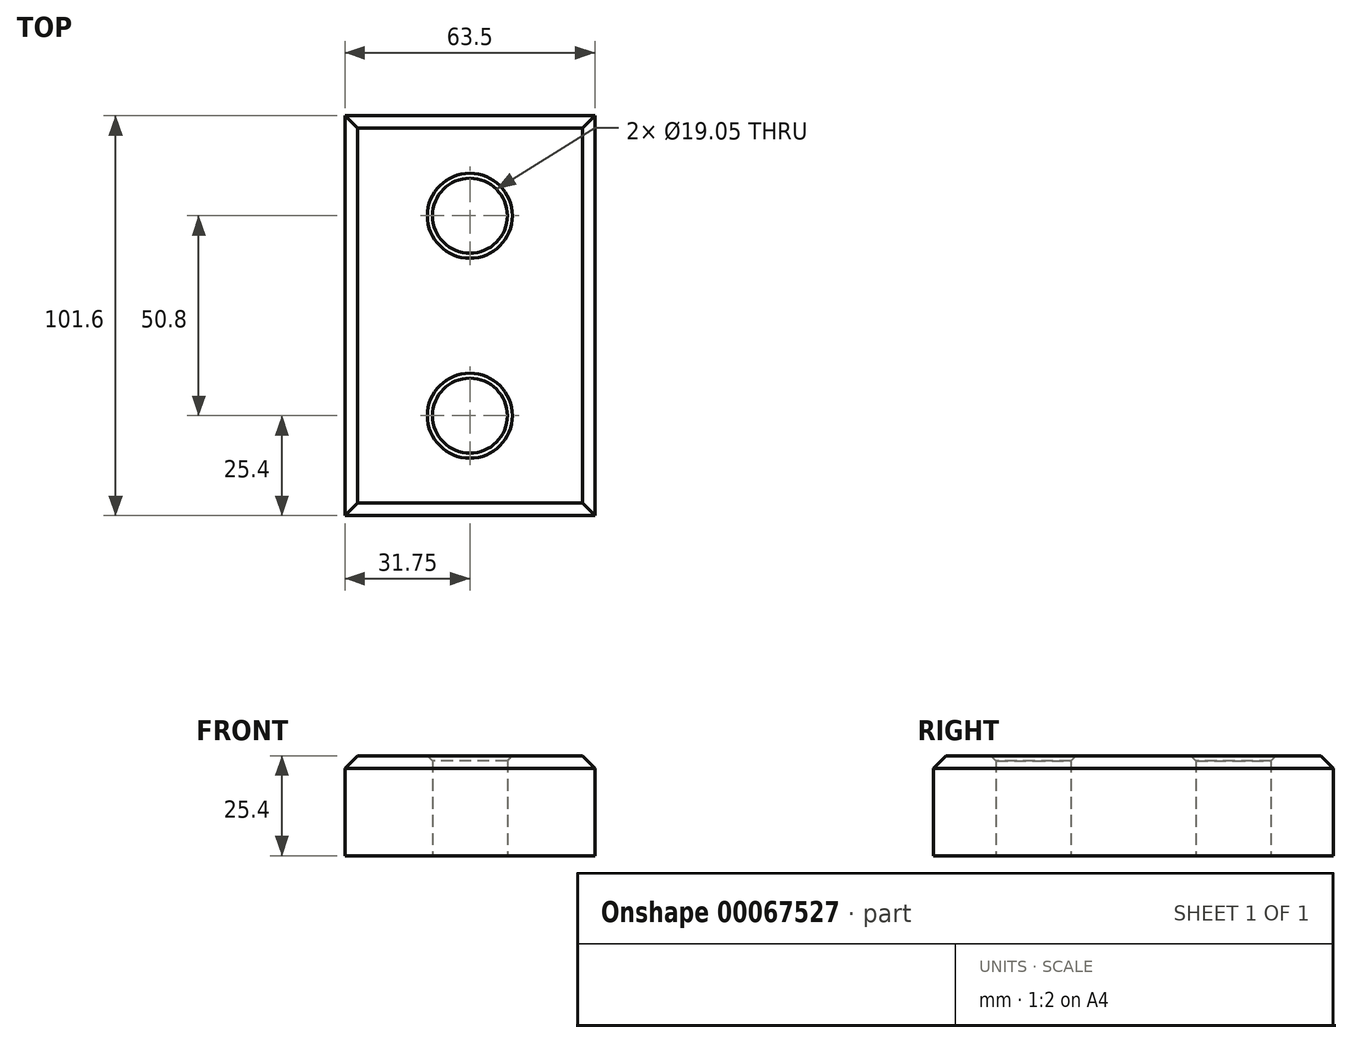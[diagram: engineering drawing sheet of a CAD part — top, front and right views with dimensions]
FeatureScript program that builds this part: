
annotation { "Feature Type Name" : "Feature", "Feature Type Description" : "" }
export const myFeature = defineFeature(function(context is Context, id is Id, definition is map)
    precondition{}
    {
        {
            var Q0;
            Q0=qCreatedBy(makeId("Top.planeOp"),FACE);
            var sketch = newSketch(context, id + "F0", { "sketchPlane" : qUnion([Q0])});
            skLineSegment(sketch, "E0.bottom", {"start": v(0, 0) * mm, "end": v(63.5, 0) * mm});
            skLineSegment(sketch, "E0.top", {"start": v(0, 101.6) * mm, "end": v(63.5, 101.6) * mm});
            skLineSegment(sketch, "E0.left", {"start": v(0, 0) * mm, "end": v(0, 101.6) * mm});
            skLineSegment(sketch, "E0.right", {"start": v(63.5, 0) * mm, "end": v(63.5, 101.6) * mm});
            skCircle(sketch, "E1", {"center": v(31.75, 76.2) * mm, "radius": 9.53 * mm});
            skCircle(sketch, "E2", {"center": v(31.75, 25.4) * mm, "radius": 9.53 * mm});
            skSolve(sketch);
        }
        {
            var Q0;
            Q0=makeQuery(id+"F0.imprint","IMPRINT",FACE,{"disambiguationData":[TD([[makeQuery(id+"F0.imprint","IMPRINT",EDGE,{"derivedFrom":sQuery(id+"F0.wireOp",EDGE,"E0.bottom")}),1.0]])]});
            extrude(context, id + "F1", {"entities" : qUnion([Q0]), "depth" : 25.4 * mm});
        }
        {
            var Q0;
            Q0=makeQuery(id+"F1.opExtrude","CAP_EDGE",EDGE,{"disambiguationData":[OSD([sQuery(id+"F0.wireOp",EDGE,"E0.right")])],"isStart":false});
            var Q1;
            Q1=makeQuery(id+"F1.opExtrude","CAP_EDGE",EDGE,{"disambiguationData":[OSD([sQuery(id+"F0.wireOp",EDGE,"E0.top")])],"isStart":false});
            var Q2;
            Q2=makeQuery(id+"F1.opExtrude","CAP_EDGE",EDGE,{"disambiguationData":[OSD([sQuery(id+"F0.wireOp",EDGE,"E0.left")])],"isStart":false});
            var Q3;
            Q3=makeQuery(id+"F1.opExtrude","CAP_EDGE",EDGE,{"disambiguationData":[OSD([sQuery(id+"F0.wireOp",EDGE,"E0.bottom")])],"isStart":false});
            chamfer(context, id + "F2", {"entities" : qUnion([Q0, Q1, Q2, Q3]), "width" : 3.17 * mm, "tangentPropagation" : true});
        }
        {
            var Q0;
            Q0=makeQuery(id+"F1.opExtrude","CAP_EDGE",EDGE,{"disambiguationData":[OSD([sQuery(id+"F0.wireOp",EDGE,"E1")])],"isStart":false});
            var Q1;
            Q1=makeQuery(id+"F1.opExtrude","CAP_EDGE",EDGE,{"disambiguationData":[OSD([sQuery(id+"F0.wireOp",EDGE,"E2")])],"isStart":false});
            chamfer(context, id + "F3", {"entities" : qUnion([Q0, Q1]), "width" : 1.27 * mm, "tangentPropagation" : true});
        }
    });
